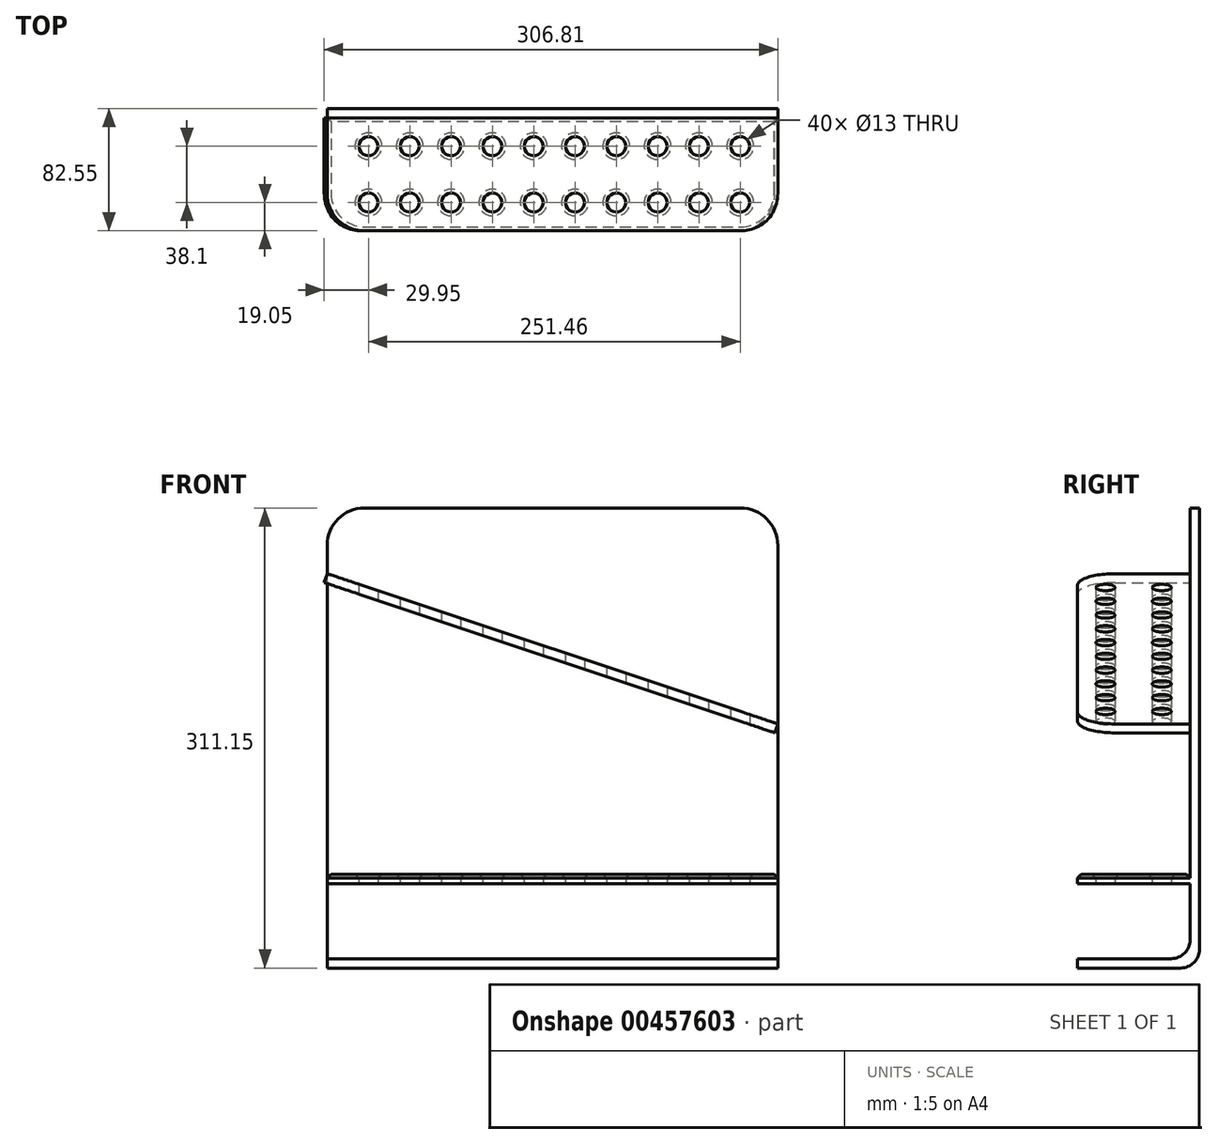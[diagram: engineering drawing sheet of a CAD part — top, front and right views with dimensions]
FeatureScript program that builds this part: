
annotation { "Feature Type Name" : "Feature", "Feature Type Description" : "" }
export const myFeature = defineFeature(function(context is Context, id is Id, definition is map)
    precondition{}
    {
        {
            var Q0;
            Q0=qCreatedBy(makeId("Top.planeOp"),FACE);
            var sketch = newSketch(context, id + "F0", { "sketchPlane" : qUnion([Q0])});
            skLineSegment(sketch, "E0.bottom", {"start": v(25.4, 0) * mm, "end": v(279.4, 0) * mm});
            skLineSegment(sketch, "E0.top", {"start": v(0, 76.2) * mm, "end": v(304.8, 76.2) * mm});
            skLineSegment(sketch, "E0.left", {"start": v(0, 25.4) * mm, "end": v(0, 76.2) * mm});
            skLineSegment(sketch, "E0.right", {"start": v(304.8, 25.4) * mm, "end": v(304.8, 76.2) * mm});
            skCircle(sketch, "E1", {"center": v(27.94, 19.05) * mm, "radius": 6.5 * mm});
            skLineSegment(sketch, "E2", {"start": v(0, 38.1) * mm, "end": v(304.8, 38.1) * mm, "construction": true});
            skCircle(sketch, "E3.MirrorC", {"center": v(27.94, 57.15) * mm, "radius": 6.5 * mm});
            skCircle(sketch, "E4.1.0.0", {"center": v(55.88, 57.15) * mm, "radius": 6.5 * mm});
            skCircle(sketch, "E4.1.0.1", {"center": v(55.88, 19.05) * mm, "radius": 6.5 * mm});
            skCircle(sketch, "E4.2.0.0", {"center": v(83.82, 57.15) * mm, "radius": 6.5 * mm});
            skCircle(sketch, "E4.2.0.1", {"center": v(83.82, 19.05) * mm, "radius": 6.5 * mm});
            skCircle(sketch, "E4.3.0.0", {"center": v(111.76, 57.15) * mm, "radius": 6.5 * mm});
            skCircle(sketch, "E4.3.0.1", {"center": v(111.76, 19.05) * mm, "radius": 6.5 * mm});
            skCircle(sketch, "E4.4.0.0", {"center": v(139.7, 57.15) * mm, "radius": 6.5 * mm});
            skCircle(sketch, "E4.4.0.1", {"center": v(139.7, 19.05) * mm, "radius": 6.5 * mm});
            skCircle(sketch, "E4.5.0.0", {"center": v(167.64, 57.15) * mm, "radius": 6.5 * mm});
            skCircle(sketch, "E4.5.0.1", {"center": v(167.64, 19.05) * mm, "radius": 6.5 * mm});
            skCircle(sketch, "E4.6.0.0", {"center": v(195.58, 57.15) * mm, "radius": 6.5 * mm});
            skCircle(sketch, "E4.6.0.1", {"center": v(195.58, 19.05) * mm, "radius": 6.5 * mm});
            skCircle(sketch, "E4.7.0.0", {"center": v(223.52, 57.15) * mm, "radius": 6.5 * mm});
            skCircle(sketch, "E4.7.0.1", {"center": v(223.52, 19.05) * mm, "radius": 6.5 * mm});
            skCircle(sketch, "E4.8.0.0", {"center": v(251.46, 57.15) * mm, "radius": 6.5 * mm});
            skCircle(sketch, "E4.8.0.1", {"center": v(251.46, 19.05) * mm, "radius": 6.5 * mm});
            skCircle(sketch, "E4.9.0.0", {"center": v(279.4, 57.15) * mm, "radius": 6.5 * mm});
            skCircle(sketch, "E4.9.0.1", {"center": v(279.4, 19.05) * mm, "radius": 6.5 * mm});
            skLineSegment(sketch, "E4.direction1", {"start": v(27.94, 19.05) * mm, "end": v(55.88, 19.05) * mm, "construction": true});
            skPoint(sketch, "E5.visualSharp", {"position": v(0, 0) * mm});
            skArc(sketch, "E5.filletArc", {"start": v(0, 25.4) * mm, "mid": v(7.44, 7.44) * mm, "end": v(25.4, 0) * mm});
            skPoint(sketch, "E6.visualSharp", {"position": v(304.8, 0) * mm});
            skArc(sketch, "E6.filletArc", {"start": v(279.4, 0) * mm, "mid": v(297.36, 7.44) * mm, "end": v(304.8, 25.4) * mm});
            skSolve(sketch);
        }
        {
            var Q0;
            Q0 = qSketchRegion(id + "F0", true);
            extrude(context, id + "F1", {"entities" : qUnion([Q0]), "depth" : 6.35 * mm});
        }
        {
            var Q0;
            Q0=makeQuery(id+"F1.opExtrude","CAP_FACE",FACE,{"disambiguationData":[OSD([sQuery(id+"F0.wireOp",EDGE,"E0.bottom"),sQuery(id+"F0.wireOp",EDGE,"E0.top"),sQuery(id+"F0.wireOp",EDGE,"E0.left"),sQuery(id+"F0.wireOp",EDGE,"E0.right"),sQuery(id+"F0.wireOp",EDGE,"E1"),sQuery(id+"F0.wireOp",EDGE,"E3.MirrorC"),sQuery(id+"F0.wireOp",EDGE,"E4.1.0.0"),sQuery(id+"F0.wireOp",EDGE,"E4.1.0.1"),sQuery(id+"F0.wireOp",EDGE,"E4.2.0.0"),sQuery(id+"F0.wireOp",EDGE,"E4.2.0.1"),sQuery(id+"F0.wireOp",EDGE,"E4.3.0.0"),sQuery(id+"F0.wireOp",EDGE,"E4.3.0.1"),sQuery(id+"F0.wireOp",EDGE,"E4.4.0.0"),sQuery(id+"F0.wireOp",EDGE,"E4.4.0.1"),sQuery(id+"F0.wireOp",EDGE,"E4.5.0.0"),sQuery(id+"F0.wireOp",EDGE,"E4.5.0.1"),sQuery(id+"F0.wireOp",EDGE,"E4.6.0.0"),sQuery(id+"F0.wireOp",EDGE,"E4.6.0.1"),sQuery(id+"F0.wireOp",EDGE,"E4.7.0.0"),sQuery(id+"F0.wireOp",EDGE,"E4.7.0.1"),sQuery(id+"F0.wireOp",EDGE,"E4.8.0.0"),sQuery(id+"F0.wireOp",EDGE,"E4.8.0.1"),sQuery(id+"F0.wireOp",EDGE,"E4.9.0.0"),sQuery(id+"F0.wireOp",EDGE,"E4.9.0.1"),sQuery(id+"F0.wireOp",EDGE,"E5.filletArc"),sQuery(id+"F0.wireOp",EDGE,"E6.filletArc")])],"isStart":false});
            chamfer(context, id + "F2", {"entities" : qUnion([Q0]), "width" : 2.54 * mm, "tangentPropagation" : true});
        }
        {
            var Q0;
            Q0=qCreatedBy(makeId("Right.planeOp"),FACE);
            var sketch = newSketch(context, id + "F3", { "sketchPlane" : qUnion([Q0])});
            skLineSegment(sketch, "E7", {"start": v(76.2, 0) * mm, "end": v(76.2, 254) * mm});
            skLineSegment(sketch, "E8", {"start": v(76.2, 0) * mm, "end": v(76.2, -50.8) * mm});
            skLineSegment(sketch, "E9", {"start": v(76.2, -50.8) * mm, "end": v(0, -50.8) * mm});
            skLineSegment(sketch, "E10", {"start": v(76.2, 254) * mm, "end": v(82.55, 254) * mm});
            skLineSegment(sketch, "E11", {"start": v(82.55, 254) * mm, "end": v(82.55, -57.15) * mm});
            skLineSegment(sketch, "E12", {"start": v(82.55, -57.15) * mm, "end": v(0, -57.15) * mm});
            skLineSegment(sketch, "E13", {"start": v(0, -57.15) * mm, "end": v(0, -50.8) * mm});
            skSolve(sketch);
        }
        {
            var Q0;
            Q0 = qSketchRegion(id + "F3", true);
            extrude(context, id + "F4", {"entities" : qUnion([Q0]), "operationType" : NewBodyOperationType.ADD, "depth" : 304.8 * mm});
        }
        {
            var Q0;
            Q0=makeQuery(id+"F4.opExtrude","SWEPT_EDGE",EDGE,{"disambiguationData":[OSD([sQuery(id+"F3.wireOp",EDGE,"E8"),sQuery(id+"F3.wireOp",EDGE,"E9")])]});
            var Q1;
            Q1=makeQuery(id+"F4.opExtrude","SWEPT_EDGE",EDGE,{"disambiguationData":[OSD([sQuery(id+"F3.wireOp",EDGE,"E11"),sQuery(id+"F3.wireOp",EDGE,"E12")])]});
            fillet(context, id + "F5", {"entities" : qUnion([Q0, Q1]), "radius" : 12.7 * mm, "tangentPropagation" : true, "allowEdgeOverflow" : false});
        }
        {
            var Q0;
            Q0=makeQuery(id+"F4.opExtrude","CAP_EDGE",EDGE,{"disambiguationData":[OSD([sQuery(id+"F3.wireOp",EDGE,"E10")])],"isStart":false});
            var Q1;
            Q1=makeQuery(id+"F4.opExtrude","CAP_EDGE",EDGE,{"disambiguationData":[OSD([sQuery(id+"F3.wireOp",EDGE,"E10")])],"isStart":true});
            fillet(context, id + "F6", {"entities" : qUnion([Q0, Q1]), "radius" : 25.4 * mm, "tangentPropagation" : true, "allowEdgeOverflow" : false});
        }
        {
            var Q0;
            {var subQ6=sQuery(id+"F3.wireOp",EDGE,"E8");var subQ7=sQuery(id+"F3.wireOp",EDGE,"E7");Q0=makeQuery(id+"F4.boolean.opBoolean","SPLIT",FACE,{"disambiguationData":[TD([makeQuery(id+"F2.opChamfer","BLEND_FACE",FACE,{"disambiguationData":[OSD([sQuery(id+"F0.wireOp",EDGE,"E0.top")])]})])],"derivedFrom":makeQuery(id+"F4.opExtrude","SWEPT_FACE",FACE,{"disambiguationData":[OSD([subQ7,subQ6])]})});}
            var sketch = newSketch(context, id + "F7", { "sketchPlane" : qUnion([Q0])});
            skLineSegment(sketch, "E14", {"start": v(0, 209.55) * mm, "end": v(304.8, 107.95) * mm});
            skLineSegment(sketch, "E15.0", {"start": v(-2, 203.53) * mm, "end": v(302.8, 101.93) * mm});
            skLineSegment(sketch, "E16", {"start": v(0, 209.55) * mm, "end": v(-2, 203.53) * mm});
            skLineSegment(sketch, "E17", {"start": v(302.8, 101.93) * mm, "end": v(304.8, 107.95) * mm});
            skSolve(sketch);
        }
        {
            var Q0;
            Q0 = qSketchRegion(id + "F7", true);
            extrude(context, id + "F8", {"entities" : qUnion([Q0]), "operationType" : NewBodyOperationType.ADD, "depth" : 76.2 * mm});
        }
        {
            var Q0;
            Q0=makeQuery(id+"F4.opExtrude","CAP_EDGE",EDGE,{"disambiguationData":[OSD([sQuery(id+"F3.wireOp",EDGE,"E13")])],"isStart":false});
            var Q1;
            Q1=makeQuery(id+"F4.opExtrude","CAP_EDGE",EDGE,{"disambiguationData":[OSD([sQuery(id+"F3.wireOp",EDGE,"E13")])],"isStart":true});
            var Q2;
            Q2=makeQuery(id+"F8.opExtrude","CAP_EDGE",EDGE,{"disambiguationData":[OSD([sQuery(id+"F7.wireOp",EDGE,"E16")])],"isStart":false});
            var Q3;
            Q3=makeQuery(id+"F8.opExtrude","CAP_EDGE",EDGE,{"disambiguationData":[OSD([sQuery(id+"F7.wireOp",EDGE,"E17")])],"isStart":false});
            fillet(context, id + "F9", {"entities" : qUnion([Q0, Q1, Q2, Q3]), "radius" : 25.4 * mm, "tangentPropagation" : true, "allowEdgeOverflow" : false});
        }
        {
            var Q0;
            Q0=makeQuery(id+"F1.opExtrude","CAP_FACE",FACE,{"disambiguationData":[OSD([sQuery(id+"F0.wireOp",EDGE,"E0.bottom"),sQuery(id+"F0.wireOp",EDGE,"E0.top"),sQuery(id+"F0.wireOp",EDGE,"E0.left"),sQuery(id+"F0.wireOp",EDGE,"E0.right"),sQuery(id+"F0.wireOp",EDGE,"E1"),sQuery(id+"F0.wireOp",EDGE,"E3.MirrorC"),sQuery(id+"F0.wireOp",EDGE,"E4.1.0.0"),sQuery(id+"F0.wireOp",EDGE,"E4.1.0.1"),sQuery(id+"F0.wireOp",EDGE,"E4.2.0.0"),sQuery(id+"F0.wireOp",EDGE,"E4.2.0.1"),sQuery(id+"F0.wireOp",EDGE,"E4.3.0.0"),sQuery(id+"F0.wireOp",EDGE,"E4.3.0.1"),sQuery(id+"F0.wireOp",EDGE,"E4.4.0.0"),sQuery(id+"F0.wireOp",EDGE,"E4.4.0.1"),sQuery(id+"F0.wireOp",EDGE,"E4.5.0.0"),sQuery(id+"F0.wireOp",EDGE,"E4.5.0.1"),sQuery(id+"F0.wireOp",EDGE,"E4.6.0.0"),sQuery(id+"F0.wireOp",EDGE,"E4.6.0.1"),sQuery(id+"F0.wireOp",EDGE,"E4.7.0.0"),sQuery(id+"F0.wireOp",EDGE,"E4.7.0.1"),sQuery(id+"F0.wireOp",EDGE,"E4.8.0.0"),sQuery(id+"F0.wireOp",EDGE,"E4.8.0.1"),sQuery(id+"F0.wireOp",EDGE,"E4.9.0.0"),sQuery(id+"F0.wireOp",EDGE,"E4.9.0.1"),sQuery(id+"F0.wireOp",EDGE,"E5.filletArc"),sQuery(id+"F0.wireOp",EDGE,"E6.filletArc")])],"isStart":false});
            var sketch = newSketch(context, id + "F10", { "sketchPlane" : qUnion([Q0])});
            skCircle(sketch, "E18.0", {"center": v(27.94, 57.15) * mm, "radius": 6.5 * mm});
            skCircle(sketch, "E18.1", {"center": v(27.94, 19.05) * mm, "radius": 6.5 * mm});
            skCircle(sketch, "E18.2", {"center": v(55.88, 57.15) * mm, "radius": 6.5 * mm});
            skCircle(sketch, "E18.3", {"center": v(55.88, 19.05) * mm, "radius": 6.5 * mm});
            skCircle(sketch, "E18.4", {"center": v(83.82, 57.15) * mm, "radius": 6.5 * mm});
            skCircle(sketch, "E18.5", {"center": v(111.76, 57.15) * mm, "radius": 6.5 * mm});
            skCircle(sketch, "E18.6", {"center": v(83.82, 19.05) * mm, "radius": 6.5 * mm});
            skCircle(sketch, "E18.7", {"center": v(111.76, 19.05) * mm, "radius": 6.5 * mm});
            skCircle(sketch, "E18.8", {"center": v(139.7, 19.05) * mm, "radius": 6.5 * mm});
            skCircle(sketch, "E18.9", {"center": v(139.7, 57.15) * mm, "radius": 6.5 * mm});
            skCircle(sketch, "E18.10", {"center": v(167.64, 57.15) * mm, "radius": 6.5 * mm});
            skCircle(sketch, "E18.11", {"center": v(167.64, 19.05) * mm, "radius": 6.5 * mm});
            skCircle(sketch, "E18.12", {"center": v(195.58, 19.05) * mm, "radius": 6.5 * mm});
            skCircle(sketch, "E18.13", {"center": v(195.58, 57.15) * mm, "radius": 6.5 * mm});
            skCircle(sketch, "E18.14", {"center": v(223.52, 57.15) * mm, "radius": 6.5 * mm});
            skCircle(sketch, "E18.15", {"center": v(223.52, 19.05) * mm, "radius": 6.5 * mm});
            skCircle(sketch, "E18.16", {"center": v(251.46, 57.15) * mm, "radius": 6.5 * mm});
            skCircle(sketch, "E18.17", {"center": v(251.46, 19.05) * mm, "radius": 6.5 * mm});
            skCircle(sketch, "E18.18", {"center": v(279.4, 57.15) * mm, "radius": 6.5 * mm});
            skCircle(sketch, "E18.19", {"center": v(279.4, 19.05) * mm, "radius": 6.5 * mm});
            skSolve(sketch);
        }
        {
            var Q0;
            Q0 = qSketchRegion(id + "F10", true);
            extrude(context, id + "F11", {"entities" : qUnion([Q0]), "operationType" : NewBodyOperationType.REMOVE, "endBound" : BoundingType.THROUGH_ALL, "depth" : 25.4 * mm});
        }
    });
